# Revit family: Door-Slider-Fleetwood-3070-OXXXX
name_source: partatom
category: Doors
revit_build: Autodesk Revit 2016 (Build: 20150714_1515(x64)
units: mm (PartAtom-declared; Revit-internal decimal feet)

## family parameters
Always vertical = Yes
Cut with Voids When Loaded = No
Host = Wall
OmniClass Number = 23.30.10.00
OmniClass Title = Doors
Room Calculation Point = No
Shared = No

## types (1)
- -
    Actuator_Height = 54 "
    Analytic Construction = <None>
    Archetype_Actuator = Hardware-Archetype_Actuator-Fleetwood
    Archetype_Actuator_Switch = Hardware-Archetype_Actuator-Fleetwood
    Archetype_Fixed_Stile = No
    Archetype_Flush_Pulls = Yes
    Archetype_Flush_Pulls_Switch = Hardware-Archetype_Flush_Pull-Fleetwood
    Archetype_Flush_Pulls_Type = Hardware-Archetype_Flush_Pull-Fleetwood
    Archetype_Hardware = Yes
    Archetype_Narrow_Actuator = Hardware-Archetype_Narrow_Actuator-Fleetwood
    Archetype_Narrow_Actuator_Switch = Placeholder
    Archetype_Narrow_Fixed_Stile = No
    Archetype_Narrow_Hardware = No
    Archetype_Narrow_Pull = Hardware-Archetype_Narrow_Pull-Fleetwood
    Archetype_Narrow_Pull_Switch = Placeholder
    Bottom_Rail = 5.15 "
    CL_1_Calc = 59.8102 "
    CL_2_Calc = 59.0713 "
    CL_3_Calc = 59.0713 "
    CL_4_Calc = 59.0713 "
    Centerline_1 = 0 "
    Centerline_2 = 0 "
    Centerline_3 = 0 "
    Centerline_4 = 0 "
    Configuration = OXXXX
    Exterior Wrap Overhang = 0.5 "
    Fixed_Stile = 1.018 "
    Frame_&_Panel = Aluminum, Anodized Clear
    Function = Exterior
    Glazing = Glass
    Glazing_Thickness = 1 "
    Hardware = Stainless Steel, Brushed
    Height = 96 "
    Interior Wrap Overhang = 0.5 "
    Interlock = 2.074 "
    Lead_Stile = 3.969 "
    Manufacturer = Fleetwood Windows and Doors
    Model = 3070
    Narrow_Fixed_Stile = Yes
    Placeholder = Placeholder
    Rough Height = 96.25 "
    Rough Width = 300.5 "
    Shim_Space = 0.25 "
    Thickness = 9.54 "
    Top_Rail = 1.46 "
    URL = www.fleetwoodusa.com
    Wall Closure = By host
    Width = 300 "

## geometry (parser evidence)
native form markers: Blend x20, Sweep x20
no freeform markers — native parametric forms only
